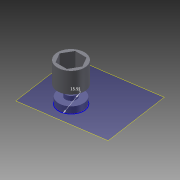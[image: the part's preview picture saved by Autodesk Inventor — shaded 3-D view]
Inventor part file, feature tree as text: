
AUTODESK INVENTOR PART (.ipt)
format: ipt  version: 2012 (Build 160160000, 160)  size: 331,264 bytes
history: native  units: mm (DEFAULTED — no unit token found)
features: sketch x8, extrude x6, plane x4, other x3, projected_geometry x2
ambient origin geometry x8: Origin, YZ Plane, XZ Plane, XY Plane, X Axis, Y Axis, Z Axis, Center Point
bodies: Solid1 (feature_tree)
feature tree (23):
  extrude  "Extrusion1"  Depth=4.0mm TaperAngle=0.0deg
  plane  "Work Plane2"
  plane  "Work Plane8"
  plane  "Work Plane9"
  other  "Spur Gear"
  extrude  "Extrusion3"  Depth=10.0mm TaperAngle=0.0deg
  extrude  "Extrusion4"  Depth=0.713998mm TaperAngle=0.0deg
  extrude  "Extrusion5"  TaperAngle=0.0deg  [1 undecoded]
  plane  "Work Plane11"
  extrude  "Extrusion6"  Depth=18.071789mm
  extrude  "Extrusion7"  Depth=5.0mm
  sketch  "Sketch9"  dims[d56=17.0mm d57=12.5mm d58=10.0mm d59=0.0mm d60=3.0mm d61=0.0mm d62=1.0mm d63=3.0mm d64=0.0mm d65=0.3mm d66=0.0mm d67=15.909903mm]
  sketch  "Sketch1"  dims[d0=15.501556mm d1=4.0mm d2=0.0mm]
  sketch  "Sketch2"  dims[d3=14.86278mm d4=10.0mm d5=0.0mm]
  other  "Srf1"
  sketch  "Sketch4"  dims[d16=18.071789mm d17=0.0mm d34=0.713998mm]
  sketch  "Sketch5"  dims[d39=0.0mm d41=0.0mm]
  projected_geometry  "Projected Loop1"
  sketch  "Sketch6"  dims[d43=18.071789mm d46=18.071789mm]
  sketch  "Sketch7"  dims[d47=0.0mm d48=0.0mm d52=5.0mm]
  projected_geometry  "Projected Loop2"
  sketch  "Sketch8"  dims[d53=10.0mm d54=0.0mm]
  other  "Pitch Diameter"
note: 1 required parameter value undecoded (feature->parameter linkage not recoverable at this tier; creation-order binding heuristic only, values carry confidence <= 0.55)
